# Revit family: Accessory-Tissue_Holder-KALLISTA-Bellis-P34608
name_source: partatom
category: Specialty Equipment
units: mm (PartAtom-declared; Revit-internal decimal feet)

## family parameters
Cut with Voids When Loaded = No
Host = Face
Maintain Annotation Orientation = No
OmniClass Number = 23.31.25.21
OmniClass Title = Toilet Paper Dispensers
Part Type = Normal
Room Calculation Point = No
Round Connector Dimension = Use Diameter
Shared = No

## types (5) — shared parameters
ADA Compliant = No
Assembly Code = C1030200
Date Modified = 05/15/2025
Default Elevation = 42"
Description = Toilet Paper Holder
Height = 2 3/8"
Length = 8"
Manufacturer = Kallista Co.
Master Format 2014 = 10 28 00
Master Format 2014 Name = Toilet, Bath, and Laundry Accessories
Material = Premium Metal Construction
Product Documentation Link = https://techcomm.kohler.com
Product Name = Bellis
URL = https://www.kallista.com
WaterSense Certified = No
Width = 3 1/2"

## per-type parameters (varying)
| type | Finish | Model | Product Page URL | Type |
| AD-Nickel Silver | Kallista-Metal-AD-Nickel_Silver | P34608-00-AD | https://www.kallista.com | 1 |
| AG-Brushed Nickel | Kallista-Metal-AG-Brushed_Nickel | P34608-00-AG |  | 2 |
| BN-Brushed Nickel | Kallista-Metal-BN-Brushed_Nickel | P34608-00-BN |  | 3 |
| CP-Chrome | Kallista-Metal-CP-Chrome | P34608-00-CP | https://www.kallista.com | 4 |
| ULB-Unlaquered Brass | Kallista-Metal-ULB-Unlaquered_Brass | P34608-00-ULB | https://www.kallista.com | 5 |

## geometry (parser evidence)
native form markers: Sweep x4
no freeform markers — native parametric forms only
